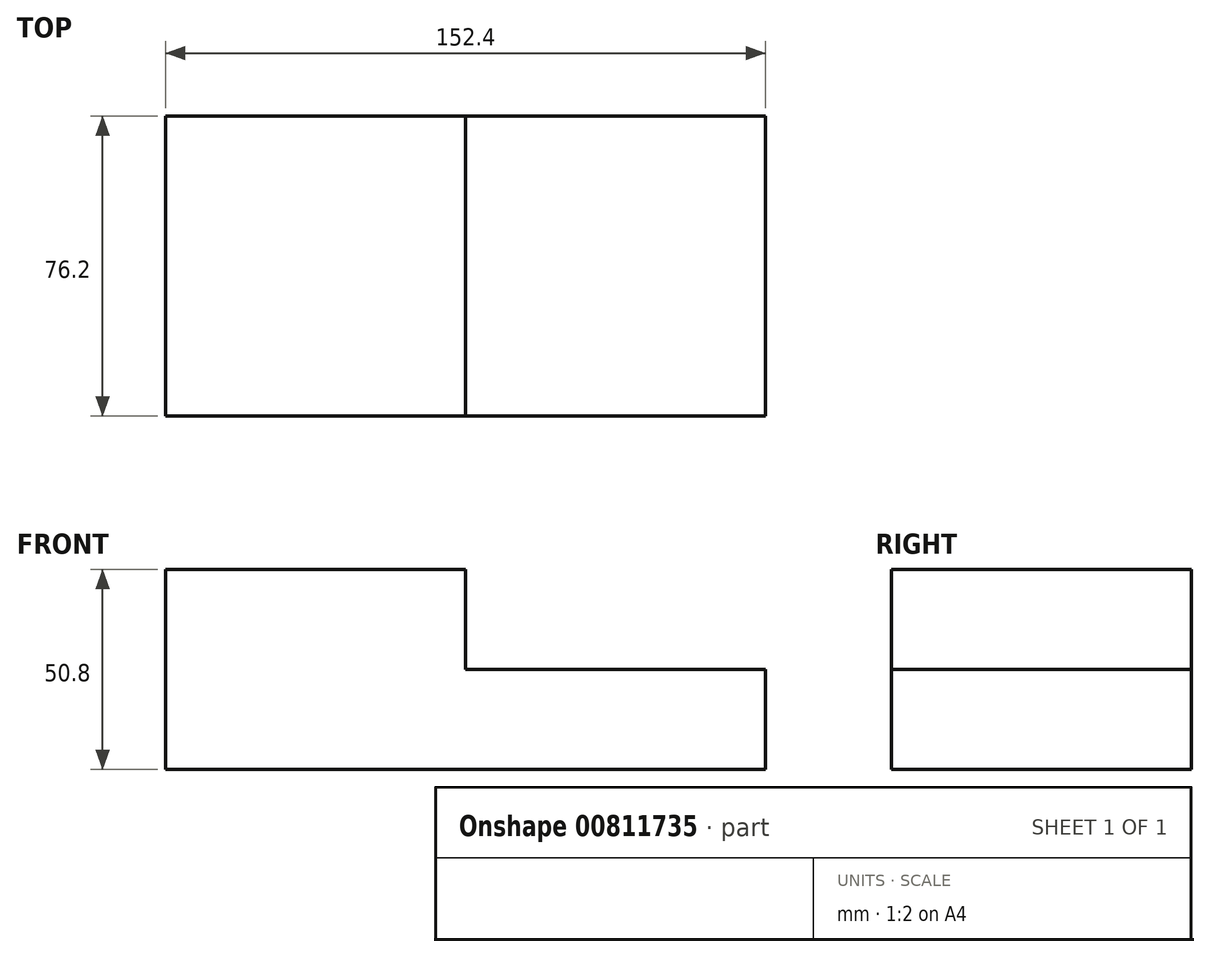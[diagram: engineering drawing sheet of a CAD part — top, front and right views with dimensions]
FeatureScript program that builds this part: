
annotation { "Feature Type Name" : "Feature", "Feature Type Description" : "" }
export const myFeature = defineFeature(function(context is Context, id is Id, definition is map)
    precondition{}
    {
        {
            var Q0;
            Q0=qCreatedBy(makeId("Front.planeOp"),FACE);
            var sketch = newSketch(context, id + "F0", { "sketchPlane" : qUnion([Q0])});
            skLineSegment(sketch, "E0", {"start": v(-62.2, 9.25) * mm, "end": v(90.2, 9.25) * mm});
            skLineSegment(sketch, "E1", {"start": v(-62.2, 9.25) * mm, "end": v(-62.2, 60.05) * mm});
            skLineSegment(sketch, "E2", {"start": v(-62.2, 60.05) * mm, "end": v(14, 60.05) * mm});
            skLineSegment(sketch, "E3", {"start": v(14, 60.05) * mm, "end": v(14, 34.65) * mm});
            skLineSegment(sketch, "E4", {"start": v(14, 34.65) * mm, "end": v(90.2, 34.65) * mm});
            skLineSegment(sketch, "E5", {"start": v(90.2, 34.65) * mm, "end": v(90.2, 9.25) * mm});
            skSolve(sketch);
        }
        {
            var Q0;
            Q0=makeQuery(id+"F0.imprint","IMPRINT",FACE,{"disambiguationData":[TD([[makeQuery(id+"F0.imprint","IMPRINT",EDGE,{"derivedFrom":sQuery(id+"F0.wireOp",EDGE,"E0")}),1.0]])]});
            extrude(context, id + "F1", {"entities" : qUnion([Q0]), "depth" : 76.2 * mm, "offsetDistance" : 25.4 * mm});
        }
    });
